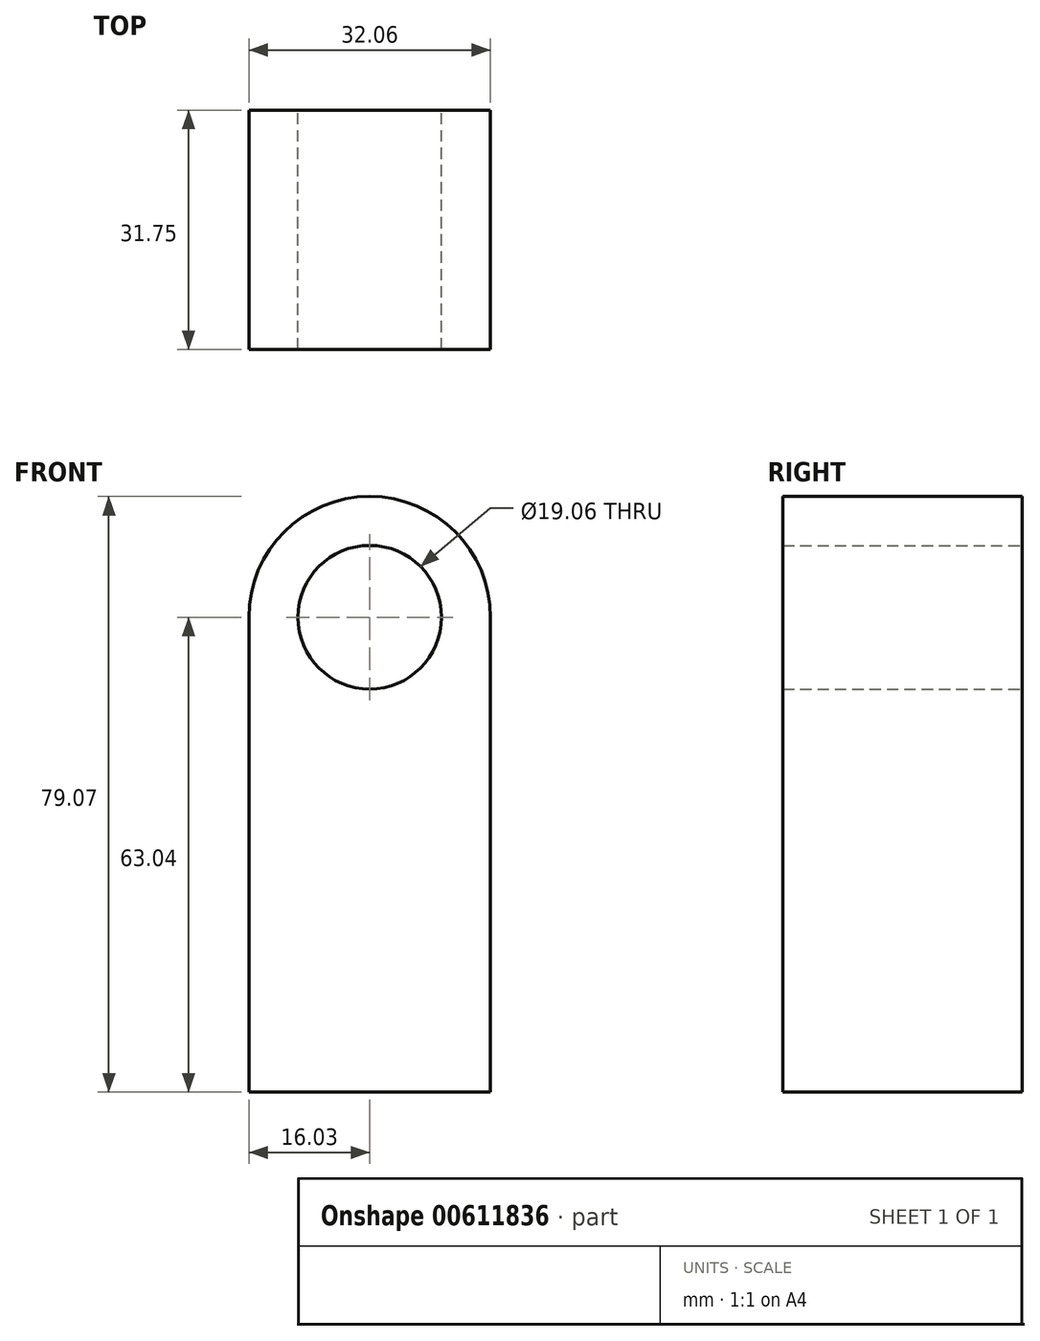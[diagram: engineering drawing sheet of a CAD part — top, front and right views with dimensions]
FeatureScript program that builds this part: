
annotation { "Feature Type Name" : "Feature", "Feature Type Description" : "" }
export const myFeature = defineFeature(function(context is Context, id is Id, definition is map)
    precondition{}
    {
        {
            var Q0;
            Q0=qCreatedBy(makeId("Front.planeOp"),FACE);
            var sketch = newSketch(context, id + "F0", { "sketchPlane" : qUnion([Q0])});
            skLineSegment(sketch, "E0.top", {"start": v(-16.03, -31.52) * mm, "end": v(16.03, -31.52) * mm});
            skLineSegment(sketch, "E0.left", {"start": v(-16.03, 31.52) * mm, "end": v(-16.03, -31.52) * mm});
            skLineSegment(sketch, "E0.right", {"start": v(16.03, 31.52) * mm, "end": v(16.03, -31.52) * mm});
            skPoint(sketch, "E0.middle", {"position": v(0, 0) * mm});
            skCircle(sketch, "E1", {"center": v(0, 31.52) * mm, "radius": 9.53 * mm});
            skArc(sketch, "E2", {"start": v(-16.03, 31.52) * mm, "mid": v(0, 47.55) * mm, "end": v(16.03, 31.52) * mm});
            skSolve(sketch);
        }
        {
            var Q0;
            Q0=makeQuery(id+"F0.imprint","IMPRINT",FACE,{"disambiguationData":[TD([[makeQuery(id+"F0.imprint","IMPRINT",EDGE,{"derivedFrom":sQuery(id+"F0.wireOp",EDGE,"E0.top")}),1.0]])]});
            extrude(context, id + "F1", {"entities" : qUnion([Q0]), "depth" : 31.75 * mm, "offsetDistance" : 25.4 * mm});
        }
    });
